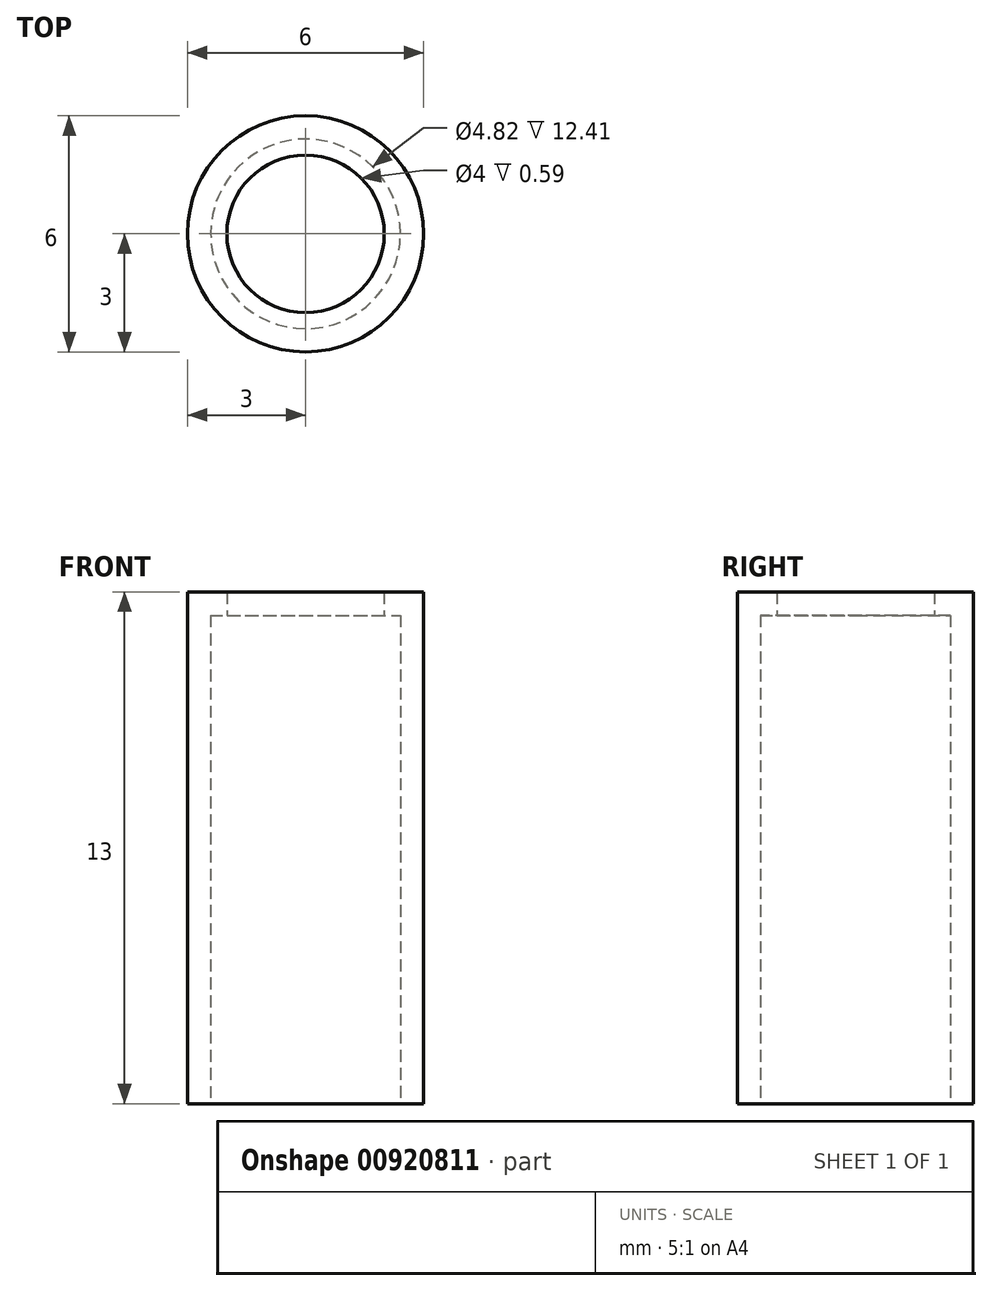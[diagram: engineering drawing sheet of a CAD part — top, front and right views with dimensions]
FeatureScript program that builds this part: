
annotation { "Feature Type Name" : "Feature", "Feature Type Description" : "" }
export const myFeature = defineFeature(function(context is Context, id is Id, definition is map)
    precondition{}
    {
        {
            var Q0;
            Q0=qCreatedBy(makeId("Front.planeOp"),FACE);
            var sketch = newSketch(context, id + "F0", { "sketchPlane" : qUnion([Q0])});
            skLineSegment(sketch, "E0", {"start": v(-21.87, 12.46) * mm, "end": v(-21.87, -0.54) * mm});
            skLineSegment(sketch, "E1", {"start": v(-21.87, 12.46) * mm, "end": v(-20.87, 12.46) * mm});
            skLineSegment(sketch, "E2", {"start": v(-20.87, 12.46) * mm, "end": v(-20.87, 11.87) * mm});
            skLineSegment(sketch, "E3", {"start": v(-20.87, 11.87) * mm, "end": v(-21.28, 11.87) * mm});
            skLineSegment(sketch, "E4", {"start": v(-21.28, 11.87) * mm, "end": v(-21.28, -0.54) * mm});
            skLineSegment(sketch, "E5", {"start": v(-21.28, -0.54) * mm, "end": v(-21.87, -0.54) * mm});
            skLineSegment(sketch, "E6", {"start": v(-21.87, 7.8) * mm, "end": v(-18.87, 7.8) * mm, "construction": true});
            skLineSegment(sketch, "E7", {"start": v(-18.87, 7.8) * mm, "end": v(-18.87, 12.46) * mm, "construction": true});
            skSolve(sketch);
        }
        {
            var Q0;
            Q0=makeQuery(id+"F0.imprint","IMPRINT",FACE,{"disambiguationData":[TD([[makeQuery(id+"F0.imprint","IMPRINT",EDGE,{"derivedFrom":sQuery(id+"F0.wireOp",EDGE,"E0")}),1.0]])]});
            var Q1;
            Q1=sQuery(id+"F0.wireOp",EDGE,"E7");
            revolve(context, id + "F1", {"surfaceOperationType" : NewSurfaceOperationType.NEW, "entities" : qUnion([Q0]), "axis" : qUnion([Q1]), "revolveType" : RevolveType.FULL});
        }
    });
